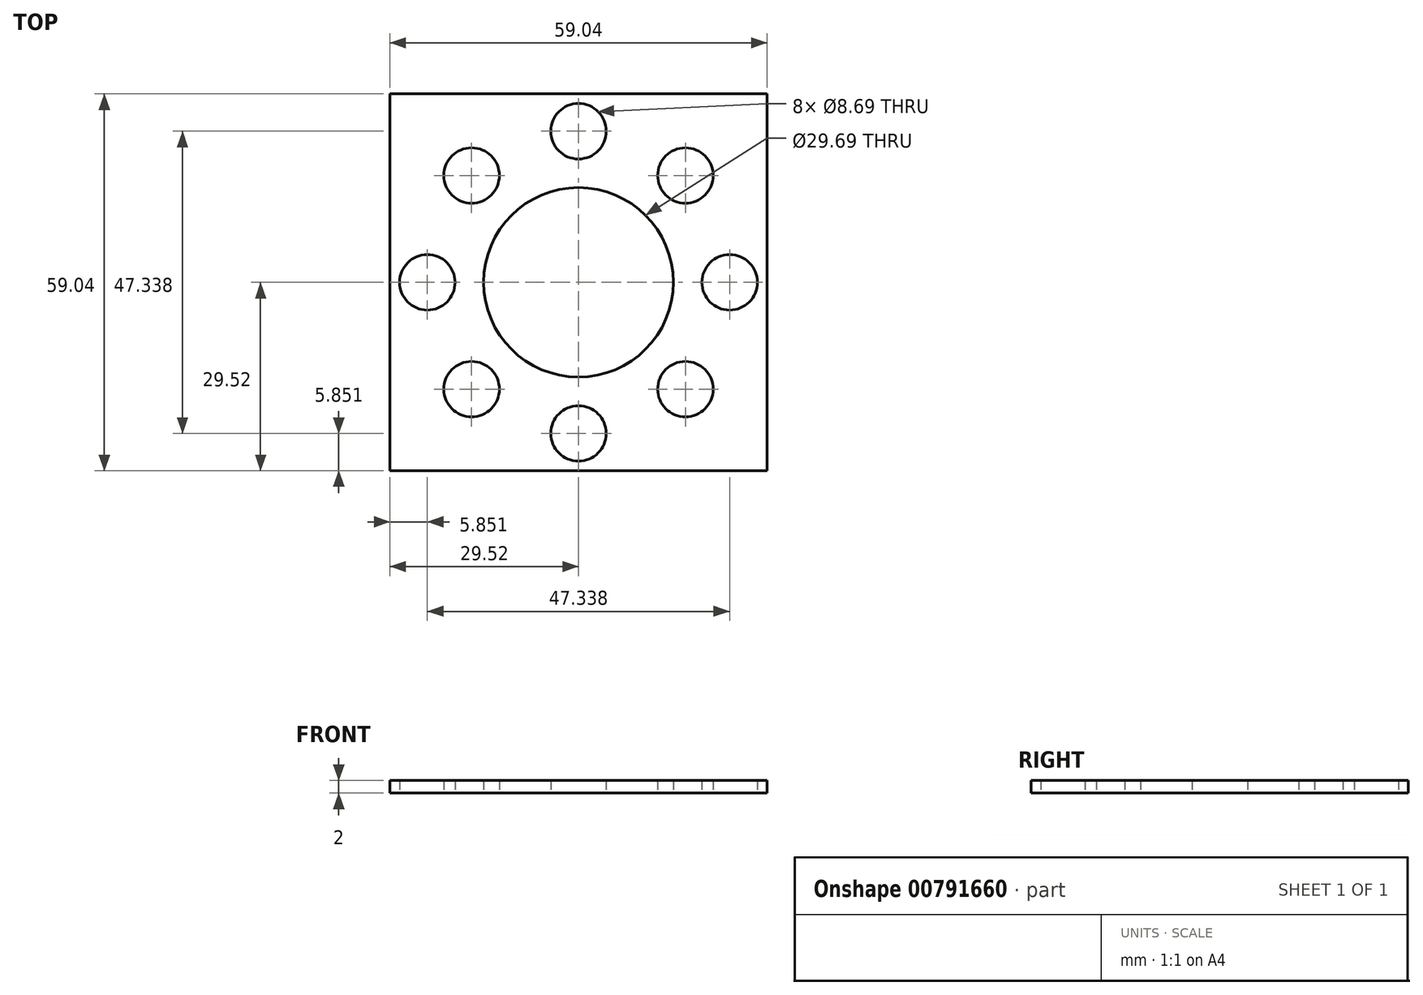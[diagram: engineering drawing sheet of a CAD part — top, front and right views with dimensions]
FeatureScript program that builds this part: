
annotation { "Feature Type Name" : "Feature", "Feature Type Description" : "" }
export const myFeature = defineFeature(function(context is Context, id is Id, definition is map)
    precondition{}
    {
        {
            var Q0;
            Q0=qCreatedBy(makeId("Top.planeOp"),FACE);
            var sketch = newSketch(context, id + "F0", { "sketchPlane" : qUnion([Q0])});
            skLineSegment(sketch, "E0.bottom", {"start": v(29.52, 29.52) * mm, "end": v(-29.52, 29.52) * mm});
            skLineSegment(sketch, "E0.top", {"start": v(29.52, -29.52) * mm, "end": v(-29.52, -29.52) * mm});
            skLineSegment(sketch, "E0.left", {"start": v(29.52, 29.52) * mm, "end": v(29.52, -29.52) * mm});
            skLineSegment(sketch, "E0.right", {"start": v(-29.52, 29.52) * mm, "end": v(-29.52, -29.52) * mm});
            skPoint(sketch, "E0.middle", {"position": v(0, 0) * mm});
            skCircle(sketch, "E1", {"center": v(0, 0) * mm, "radius": 14.84 * mm});
            skCircle(sketch, "E2", {"center": v(0, 23.67) * mm, "radius": 4.34 * mm});
            skCircle(sketch, "E3.1.0", {"center": v(-16.74, 16.74) * mm, "radius": 4.34 * mm});
            skCircle(sketch, "E3.2.0", {"center": v(-23.67, 0) * mm, "radius": 4.34 * mm});
            skCircle(sketch, "E3.3.0", {"center": v(-16.74, -16.74) * mm, "radius": 4.34 * mm});
            skCircle(sketch, "E3.4.0", {"center": v(0, -23.67) * mm, "radius": 4.34 * mm});
            skCircle(sketch, "E3.5.0", {"center": v(16.74, -16.74) * mm, "radius": 4.34 * mm});
            skCircle(sketch, "E3.6.0", {"center": v(23.67, 0) * mm, "radius": 4.34 * mm});
            skCircle(sketch, "E3.7.0", {"center": v(16.74, 16.74) * mm, "radius": 4.34 * mm});
            skLineSegment(sketch, "E4", {"start": v(-29.52, -29.52) * mm, "end": v(29.52, 29.52) * mm});
            skSolve(sketch);
        }
        {
            var Q0;
            Q0 = qSketchRegion(id + "F0", true);
            extrude(context, id + "F1", {"entities" : qUnion([Q0]), "depth" : 2 * mm, "offsetDistance" : 25.4 * mm});
        }
        {
            var Q0;
            Q0=qCreatedBy(makeId("Right.planeOp"),FACE);
            cPlane(context, id + "F2", {"entities" : qUnion([Q0]), "cplaneType" : CPlaneType.OFFSET, "offset" : 29.4 * mm, "oppositeDirection" : true, "width" : 150 * mm, "height" : 150 * mm});
        }
    });
